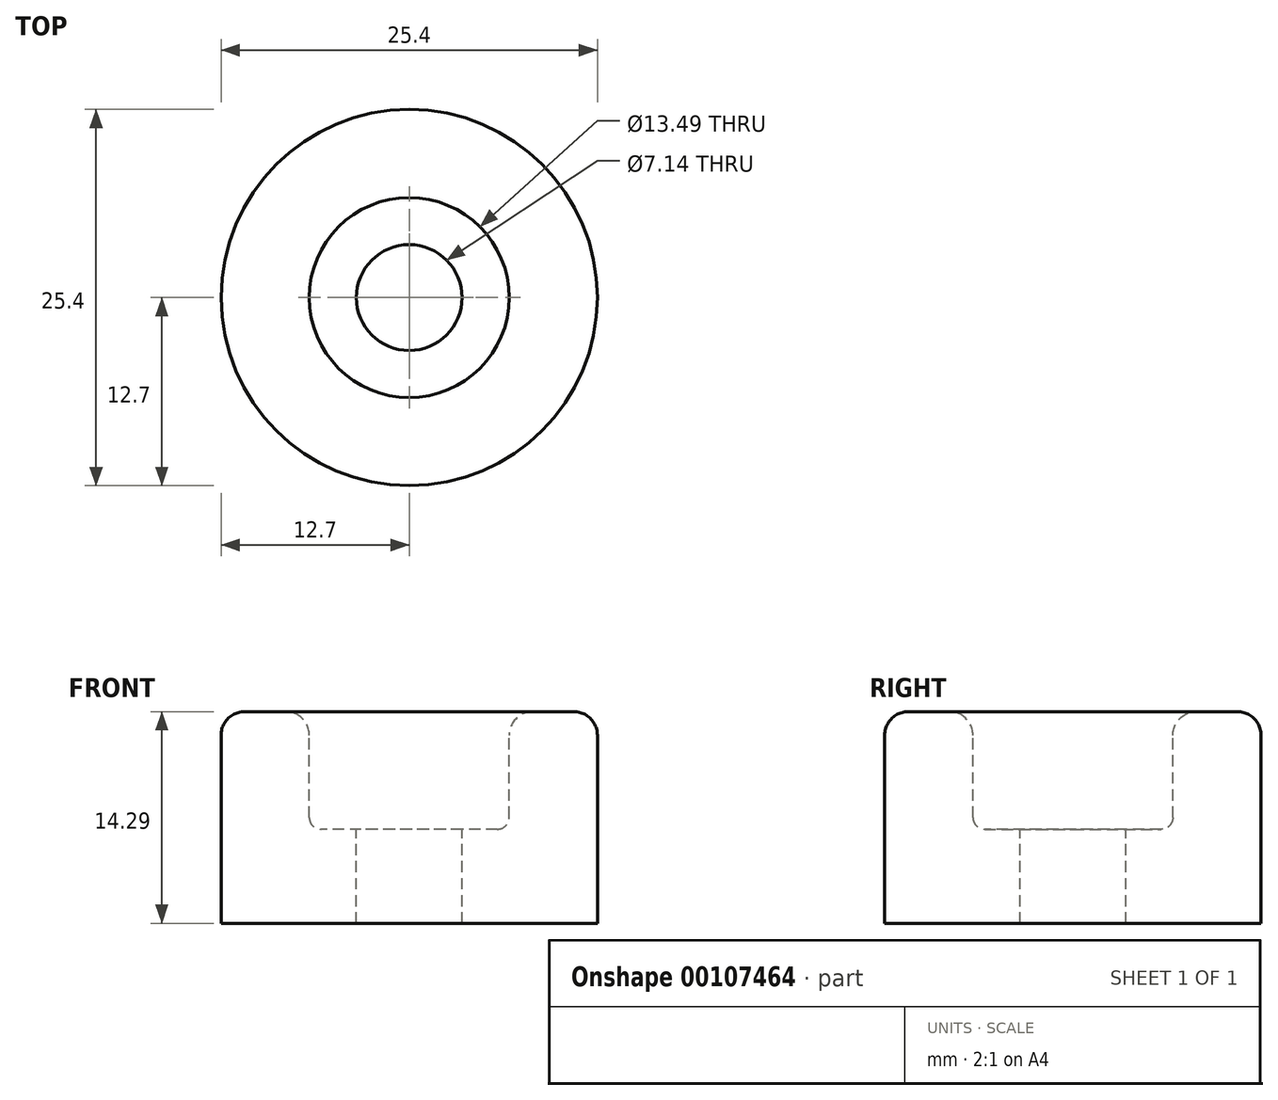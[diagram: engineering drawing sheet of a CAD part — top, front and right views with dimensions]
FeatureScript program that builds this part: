
annotation { "Feature Type Name" : "Feature", "Feature Type Description" : "" }
export const myFeature = defineFeature(function(context is Context, id is Id, definition is map)
    precondition{}
    {
        {
            var Q0;
            Q0=qCreatedBy(makeId("Front.planeOp"),FACE);
            var sketch = newSketch(context, id + "F0", { "sketchPlane" : qUnion([Q0])});
            skLineSegment(sketch, "E0", {"start": v(0, 6.35) * mm, "end": v(5.95, 6.35) * mm});
            skLineSegment(sketch, "E1", {"start": v(6.75, 7.14) * mm, "end": v(6.75, 12.7) * mm});
            skLineSegment(sketch, "E2", {"start": v(8.33, 14.29) * mm, "end": v(11.11, 14.29) * mm});
            skLineSegment(sketch, "E3", {"start": v(12.7, 12.7) * mm, "end": v(12.7, 0) * mm});
            skLineSegment(sketch, "E4", {"start": v(12.7, 0) * mm, "end": v(0, 0) * mm});
            skPoint(sketch, "E5.visualSharp", {"position": v(6.75, 14.29) * mm});
            skArc(sketch, "E5.filletArc", {"start": v(8.33, 14.29) * mm, "mid": v(7.21, 13.82) * mm, "end": v(6.75, 12.7) * mm});
            skPoint(sketch, "E6.visualSharp", {"position": v(12.7, 14.29) * mm});
            skArc(sketch, "E6.filletArc", {"start": v(12.7, 12.7) * mm, "mid": v(12.24, 13.82) * mm, "end": v(11.11, 14.29) * mm});
            skPoint(sketch, "E7.visualSharp", {"position": v(6.75, 6.35) * mm});
            skArc(sketch, "E7.filletArc", {"start": v(5.95, 6.35) * mm, "mid": v(6.51, 6.58) * mm, "end": v(6.75, 7.14) * mm});
            skLineSegment(sketch, "E8", {"start": v(0, 6.35) * mm, "end": v(0, 0) * mm});
            skSolve(sketch);
        }
        {
            var Q0;
            Q0=makeQuery(id+"F0.imprint","IMPRINT",FACE,{"disambiguationData":[TD([[makeQuery(id+"F0.imprint","IMPRINT",EDGE,{"derivedFrom":sQuery(id+"F0.wireOp",EDGE,"E0")}),-1.0]])]});
            var Q1;
            Q1=sQuery(id+"F0.wireOp",EDGE,"E8");
            revolve(context, id + "F1", {"entities" : qUnion([Q0]), "axis" : qUnion([Q1]), "revolveType" : RevolveType.FULL});
        }
        {
            var Q0;
            Q0=makeQuery(id+"F1.opRevolve","SWEPT_FACE",FACE,{"disambiguationData":[OSD([sQuery(id+"F0.wireOp",EDGE,"E0")])]});
            var sketch = newSketch(context, id + "F2", { "sketchPlane" : qUnion([Q0])});
            skCircle(sketch, "E9", {"center": v(0, 0) * mm, "radius": 3.57 * mm});
            skSolve(sketch);
        }
        {
            var Q0;
            Q0 = qSketchRegion(id + "F2", true);
            extrude(context, id + "F3", {"entities" : qUnion([Q0]), "operationType" : NewBodyOperationType.REMOVE, "endBound" : BoundingType.UP_TO_NEXT, "oppositeDirection" : true, "depth" : 25.4 * mm});
        }
    });
